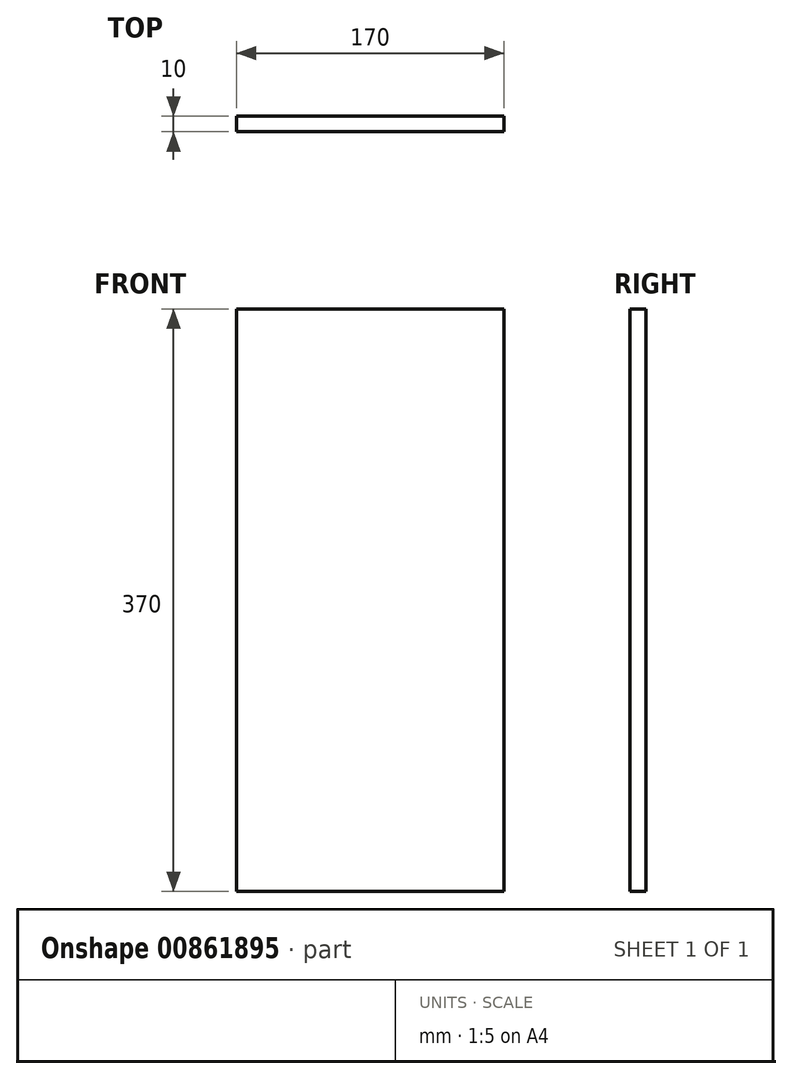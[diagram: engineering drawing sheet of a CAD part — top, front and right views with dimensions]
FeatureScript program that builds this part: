
annotation { "Feature Type Name" : "Feature", "Feature Type Description" : "" }
export const myFeature = defineFeature(function(context is Context, id is Id, definition is map)
    precondition{}
    {
        {
            var Q0;
            Q0=qCreatedBy(makeId("Front.planeOp"),FACE);
            var sketch = newSketch(context, id + "F0", { "sketchPlane" : qUnion([Q0])});
            skLineSegment(sketch, "E0.bottom", {"start": v(-150.1, -182.3) * mm, "end": v(19.9, -182.3) * mm});
            skLineSegment(sketch, "E0.top", {"start": v(-150.1, 187.7) * mm, "end": v(19.9, 187.7) * mm});
            skLineSegment(sketch, "E0.left", {"start": v(-150.1, -182.3) * mm, "end": v(-150.1, 187.7) * mm});
            skLineSegment(sketch, "E0.right", {"start": v(19.9, -182.3) * mm, "end": v(19.9, 187.7) * mm});
            skSolve(sketch);
        }
        {
            var Q0;
            Q0=makeQuery(id+"F0.imprint","IMPRINT",FACE,{"disambiguationData":[TD([[makeQuery(id+"F0.imprint","IMPRINT",EDGE,{"derivedFrom":sQuery(id+"F0.wireOp",EDGE,"E0.bottom")}),1.0]])]});
            extrude(context, id + "F1", {"entities" : qUnion([Q0]), "depth" : 10 * mm, "offsetDistance" : 25 * mm});
        }
    });
